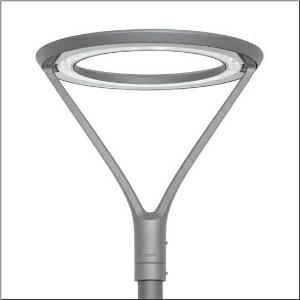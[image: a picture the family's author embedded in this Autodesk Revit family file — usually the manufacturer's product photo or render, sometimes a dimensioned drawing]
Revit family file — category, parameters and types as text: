
# Revit family: dl_20___st1_2a_5xa51283wa008p_e3b2
name_source: partatom
category: Lighting Fixtures
units: mm (PartAtom-declared; Revit-internal decimal feet)

## family parameters
Cut with Voids When Loaded = No
Host = Face
Light Source = No
Part Type = Normal
Room Calculation Point = No
Round Connector Dimension = Use Diameter
Shared = No

## types (1)
- --- (1 x LED, 4200 lm, 34.3 W, 3000K)
    Apparent Load = 34 VA
    CIE Flux Codes = 32 72 97 100 100
    Color Rendering = 70
    Color Temperature = 3000K
    Default Elevation = 1800 mm
    Description = DL® 20, mast luminaire, primary light control with reflector, highly specular, primary optical cover: cover, of toughened safety glass of clear glass with excellent transmission level, light distribution: ST1.2a, light emission: direct distribution, primary light characteristic: asymmetric, installation type: post-top, LED, High Power LED, rated luminous flux: 4.180lm, luminous efficacy: 79lm/W, light colour: 730, colour temperature: 3000K, control gear: Plus, control: overheat protection, power reduction, digital communication interface, constant luminous flux control, time-dependent luminous flux control, flexible luminous flux parameterisation, electronic power reduction, mains connection: 230..240V, 50/60Hz, connection cable pre-assembled, cable length: 5m, start of lifetime: 53W, end of service life: 54W, reduction: 24W, luminaire housing, upper part, of cast aluminium, powder-coated, Siteco® metallic grey (DB 702S), diameter: 690mm, height: 690mm, spigot size: 76mm (post-top), mounting height: 4..6m, luminaire housing, of cast aluminium, powder-coated, Siteco® metallic grey (DB 702S), equipment: Power, protection rating (complete): IP66, insulation class (complete): insulation class II (safety insulation), certification: CE, ENEC, VDE, impact resistance: IK08, permissible operating ambient temperature: -25..+30°C, standard-compliant lighting for roads and squares, packaging unit: 1 piece

Light Distribution: ST1.2a
    Height = 690 mm
    Lamp = 1 x LED
    Lamp Light Flux = 4200 lm
    Lamp Power = 34.3 W
    Lamp count = 1
    Length = 690 mm
    Luminous efficacy = 122 lm/W
    Manufacturer = Siteco
    ModVariant = No
    Model = 5XA51283WA008P
    Number of Poles = 1
    OnlyDefault = Yes
    Power Factor = 1
    Product Name = DL 20 | ST1.2a
    Product group = mast luminaire | pylon top
    ProductGroupID = 6100
    Protection Class = Protection class II
    Protection Degree = IP 66
    RLX_Detail_Level = 1
    RLX_Emergency_Light_Flux = 0 lm
    RLX_Emergency_Type = 0
    RLX_Emergency_Type_DB = No
    RlxData = <blob elided: 206845 chars, md5=457b1392>
    Socket = socket
    Standby Power = 0 W
    System Light Flux = 4200 lm
    System Power = 34 W
    Type Comments = factory setting: luminous flux: 100 % | dim-lin: 254 | 464 mA
    Type Image = l_1006001.jpg
    URL = http://relux.com
    VarID = @adj_085155
    Voltage = 0 V
    Weight = 0.00 kg
    Width = 0 mm  [stored 0 ft]

note: [stored X ft] marks values corroborated as IEEE doubles in the binary element streams (Revit-internal decimal feet)

## geometry (parser evidence)
native form markers: Blend x4, Sweep x10
no freeform markers — native parametric forms only
